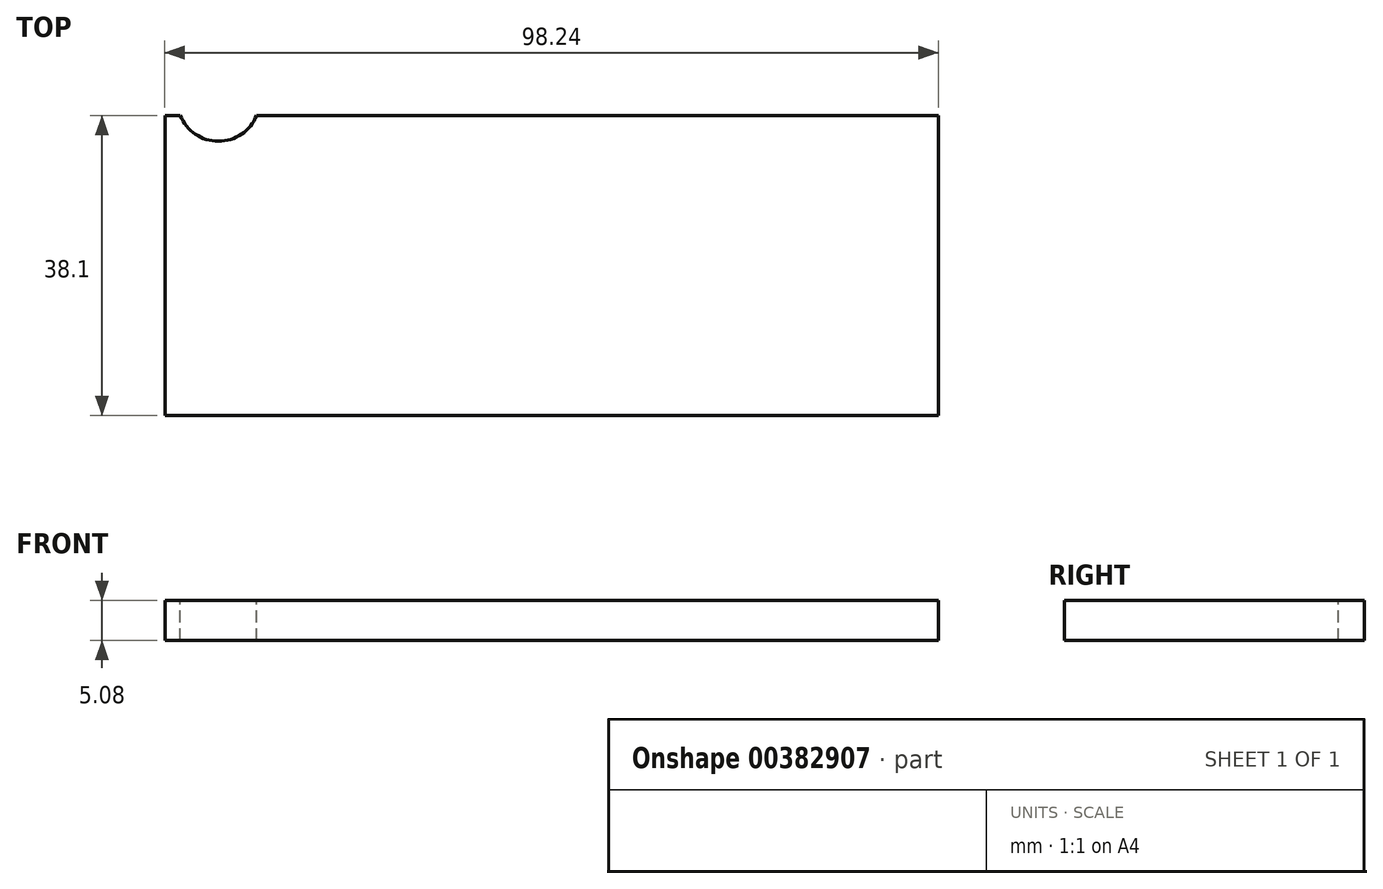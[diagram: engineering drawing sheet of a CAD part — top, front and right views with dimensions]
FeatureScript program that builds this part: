
annotation { "Feature Type Name" : "Feature", "Feature Type Description" : "" }
export const myFeature = defineFeature(function(context is Context, id is Id, definition is map)
    precondition{}
    {
        {
            var Q0;
            Q0=qCreatedBy(makeId("Top.planeOp"),FACE);
            var sketch = newSketch(context, id + "F0", { "sketchPlane" : qUnion([Q0])});
            skLineSegment(sketch, "E0.bottom", {"start": v(-48.85, -1.97) * mm, "end": v(49.39, -1.97) * mm});
            skLineSegment(sketch, "E0.top", {"start": v(-48.85, -40.07) * mm, "end": v(49.39, -40.07) * mm});
            skLineSegment(sketch, "E0.left", {"start": v(-48.85, -1.97) * mm, "end": v(-48.85, -40.07) * mm});
            skLineSegment(sketch, "E0.right", {"start": v(49.39, -1.97) * mm, "end": v(49.39, -40.07) * mm});
            skSolve(sketch);
        }
        {
            var Q0;
            Q0=makeQuery(id+"F0.imprint","IMPRINT",FACE,{"disambiguationData":[TD([[makeQuery(id+"F0.imprint","IMPRINT",EDGE,{"derivedFrom":sQuery(id+"F0.wireOp",EDGE,"E0.bottom")}),-1.0]])]});
            extrude(context, id + "F1", {"entities" : qUnion([Q0]), "depth" : 5.08 * mm});
        }
        {
            var Q0;
            Q0=makeQuery(id+"F1.opExtrude","CAP_FACE",FACE,{"disambiguationData":[OSD([sQuery(id+"F0.wireOp",EDGE,"E0.bottom"),sQuery(id+"F0.wireOp",EDGE,"E0.top"),sQuery(id+"F0.wireOp",EDGE,"E0.left"),sQuery(id+"F0.wireOp",EDGE,"E0.right")])],"isStart":false});
            var sketch = newSketch(context, id + "F2", { "sketchPlane" : qUnion([Q0])});
            skCircle(sketch, "E1", {"center": v(-42.05, 0) * mm, "radius": 5.24 * mm});
            skSolve(sketch);
        }
        {
            var Q0;
            Q0 = qSketchRegion(id + "FLTIENFgqQON3dO_1", true);
            var Q1;
            Q1=makeQuery(id+"F2.imprint","IMPRINT",FACE,{"disambiguationData":[TD([[makeQuery(id+"F2.imprint","IMPRINT",EDGE,{"derivedFrom":sQuery(id+"F2.wireOp",EDGE,"E1")}),1.0]])]});
            extrude(context, id + "F3", {"entities" : qUnion([Q0, Q1]), "operationType" : NewBodyOperationType.REMOVE, "oppositeDirection" : true, "depth" : 25.4 * mm});
        }
    });
